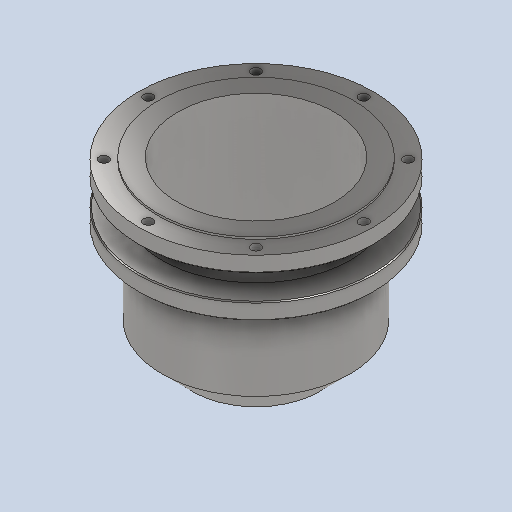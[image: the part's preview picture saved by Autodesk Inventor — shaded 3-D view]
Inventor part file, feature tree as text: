
AUTODESK INVENTOR PART (.ipt)
format: ipt  version: 2023 (Build 270158000, 158)  size: 261,120 bytes
history: native  units: mm
features: sketch x3, hole x2, pattern_circular x2, revolve x1, chamfer x1
ambient origin geometry x8: Origin, YZ Plane, XZ Plane, XY Plane, X Axis, Y Axis, Z Axis, Center Point
bodies: Solid1 (feature_tree)
feature tree (9):
  revolve  "Revolution1"  [1 undecoded]
  hole  "Hole1"  [1 undecoded]
  pattern_circular  "Circular Pattern1"  Count=2  [1 undecoded]
  chamfer  "Chamfer1"  Distance=30.0mm
  hole  "Hole2"  [1 undecoded]
  pattern_circular  "Circular Pattern2"  [2 undecoded]
  sketch  "Sketch1"  dims[d0=135.0deg d2=80.0mm]
  sketch  "Sketch2"  dims[d3=50.0mm d4=47.5mm]
  sketch  "Sketch3"  dims[d5=65.0mm d6=20.0mm d9=30.0mm d10=120.0mm d11=0.7mm d12=360.0deg d13=21.293017mm d14=55.0mm d15=4.917mm d16=12.0mm d17=4.0mm d18=2.0mm d19=90.0deg d20=17.1mm d21=20.594885mm d22=80.0mm d23=360.0deg d25=8.0mm d26=1.0mm d27=100.0mm d28=96.0mm d29=4.0mm d30=2.3mm d31=87.5mm d32=6.0mm d33=8.0mm d34=0.5mm d35=2.0mm d36=45.0deg d37=29.5mm d38=1.567mm d39=4.0mm d40=4.0mm d41=2.0mm d42=90.0deg d43=5.0mm d44=20.594885mm d45=40.0mm d46=360.0deg]
note: 6 required parameter values undecoded (feature->parameter linkage not recoverable at this tier; creation-order binding heuristic only, values carry confidence <= 0.55)